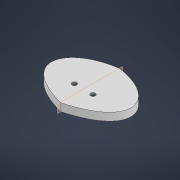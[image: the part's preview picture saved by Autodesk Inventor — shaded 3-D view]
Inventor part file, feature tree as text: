
AUTODESK INVENTOR PART (.ipt)
format: ipt  version: 2021 (Build 250183000, 183)  size: 104,960 bytes
history: native  units: mm
features: sketch x2, extrude x1, hole x1
ambient origin geometry x8: Origin, YZ Plane, XZ Plane, XY Plane, X Axis, Y Axis, Z Axis, Center Point
bodies: Solid1 (feature_tree)
feature tree (4):
  extrude  "Extrusion1"  Depth=10.0mm
  hole  "Hole1"  [1 undecoded]
  sketch  "Sketch1"  dims[d0=10.0mm d1=0.0mm d2=12.113mm]
  sketch  "Sketch2"  dims[d3=6.0mm d4=6.0mm d5=4.0mm d6=2.0mm d7=90.0deg d8=8.0mm d9=20.594885mm d10=12.113mm d11=0.0mm d12=0.0mm]
note: 1 required parameter value undecoded (feature->parameter linkage not recoverable at this tier; creation-order binding heuristic only, values carry confidence <= 0.55)
